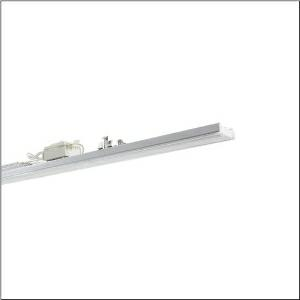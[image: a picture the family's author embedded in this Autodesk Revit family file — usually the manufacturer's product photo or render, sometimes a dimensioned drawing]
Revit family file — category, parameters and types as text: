
# Revit family: licross_r__11_recessed_ho_51te1edv4m1s_dcd1
name_source: partatom
category: Lighting Fixtures
units: mm (PartAtom-declared; Revit-internal decimal feet)

## family parameters
Cut with Voids When Loaded = No
Host = Face
Light Source = No
Part Type = Normal
Room Calculation Point = No
Round Connector Dimension = Use Diameter
Shared = No

## types (1)
- --- (1 x LED, 26450 lm, 150.5 W, 4000K)
    Apparent Load = 150 VA
    CIE Flux Codes = 85 95 99 100 100
    Color Rendering = 80
    Color Temperature = 4000K
    Default Elevation = 1800 mm
    Description = Licross® 11 Recessed HO, luminaire insert, of sheet steel, galvanised, coil coated, white, length: 2.250mm, width: 66mm, height: 67mm, LED rated luminous flux: 26.450lm, light colour: 840, control gear: DALI 2, with plug, 5-pole, with phase selection, mains connection: 220..240V, AC, 50/60Hz, rated input power: 151W, internal wiring halogen-free, primary light control with lens, of plastic, primary optical cover: cover, of PMMA, light emission: direct distribution, primary light characteristic: symmetric, protection rating (complete): IP54, insulation class (complete): insulation class I (protective earthing), certification: CE, ENEC, VDE, UKCA, protection symbol: D if used in an environment with non-conductive dust loads with corresponding accessories, impact resistance: IK06, permissible ambient temperature for indoor applications: -40..+35°C, corresponds to IFS (International Featured Standards) requirements for safety and quality in the food industry, reducing of maximum allowable ambient temperature of 5°C with ceiling mounting, LABS conformity tested according to VDMA 24364:2018-05, packaging unit: 1 piece
    Height = 58 mm
    Lamp = 1 x LED
    Lamp Light Flux = 26450 lm
    Lamp Power = 150.5 W
    Lamp count = 1
    Length = 2250 mm
    Luminous efficacy = 176 lm/W
    Manufacturer = Siteco
    ModVariant = No
    Model = 51TE1EDV4M1S
    Mounting Place = Ceiling
    Mounting Type = Pendant
    Number of Poles = 1
    OnlyDefault = Yes
    Power Factor = 1
    Product Name = Licross® 11 Recessed HO
    Product group = luminaire insert | ceiling pendant
    ProductGroupID = 902
    Protection Class = Protection class I
    Protection Degree = IP 54
    RLX_Detail_Level = 1
    RLX_Emergency_Light_Flux = 0 lm
    RLX_Emergency_Type = 0
    RLX_Emergency_Type_DB = No
    RlxData = <blob elided: 29893 chars, md5=f9b413cc>
    Socket = socket
    Standby Power = 0 W
    System Light Flux = 26450 lm
    System Power = 150 W
    Type Comments = factory setting: luminous flux: 100 % | dim-lin: 254 | 690 mA
    Type Image = l_1296930.jpg
    URL = http://relux.com
    VarID = @adj_117185
    Voltage = 0 V
    Weight = 0.00 kg
    Width = 66 mm

## geometry (parser evidence)
native form markers: Blend x4, Sweep x8
no freeform markers — native parametric forms only
